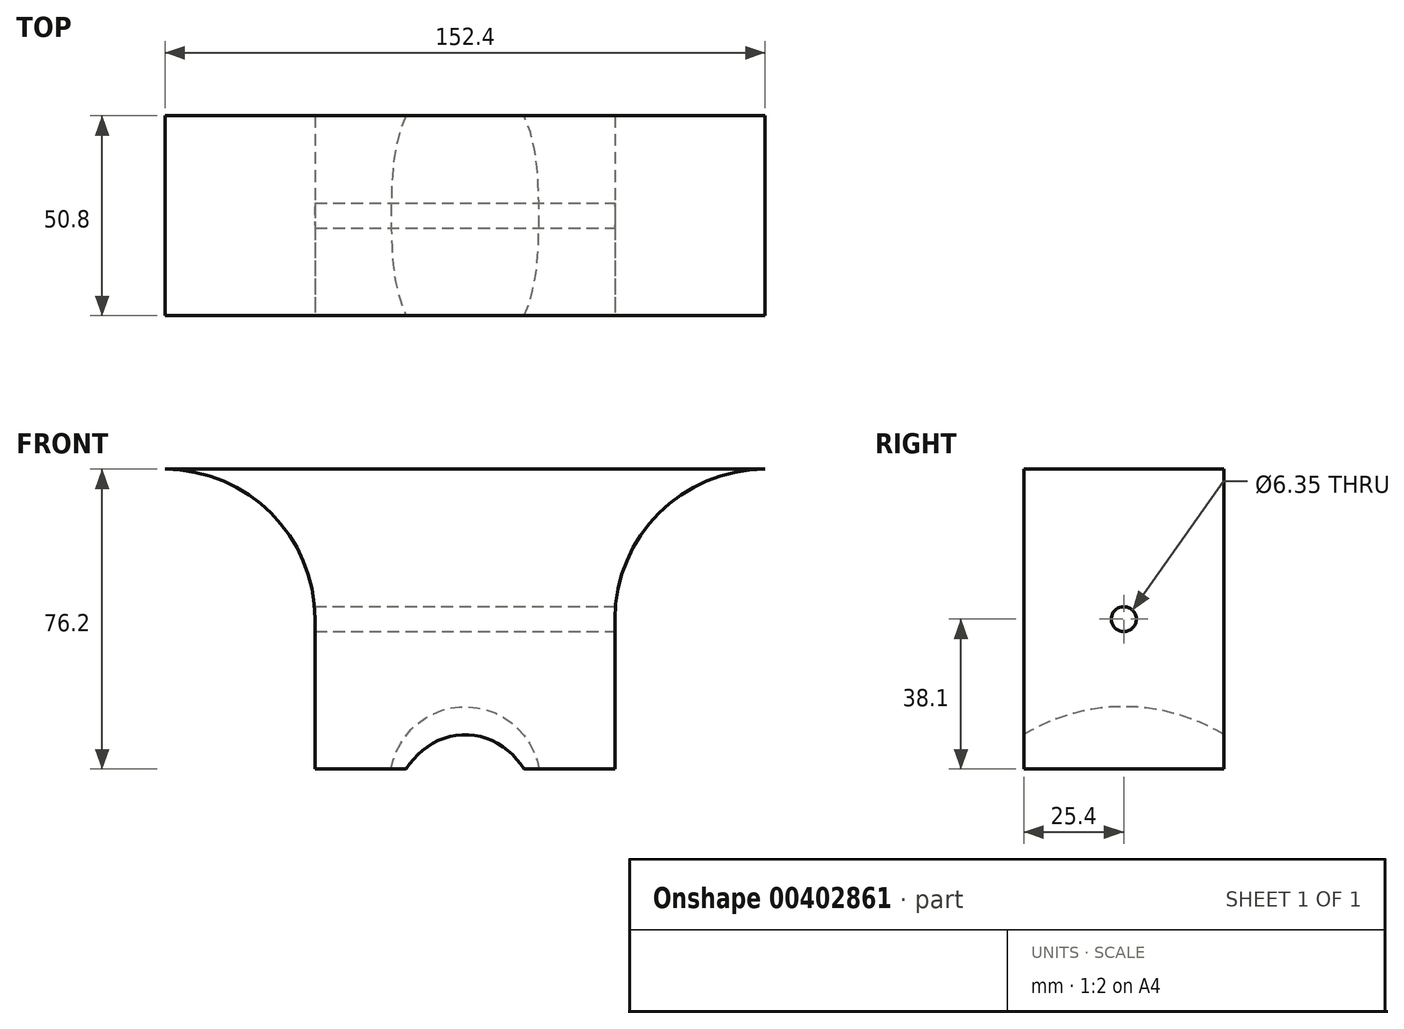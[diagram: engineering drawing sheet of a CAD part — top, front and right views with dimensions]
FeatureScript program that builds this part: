
annotation { "Feature Type Name" : "Feature", "Feature Type Description" : "" }
export const myFeature = defineFeature(function(context is Context, id is Id, definition is map)
    precondition{}
    {
        {
            var Q0;
            Q0=qCreatedBy(makeId("Front.planeOp"),FACE);
            var sketch = newSketch(context, id + "F0", { "sketchPlane" : qUnion([Q0])});
            skLineSegment(sketch, "E0.bottom", {"start": v(76.2, 38.1) * mm, "end": v(-76.2, 38.1) * mm});
            skLineSegment(sketch, "E0.top", {"start": v(76.2, -38.1) * mm, "end": v(-76.2, -38.1) * mm});
            skLineSegment(sketch, "E0.left", {"start": v(76.2, 38.1) * mm, "end": v(76.2, -38.1) * mm});
            skLineSegment(sketch, "E0.right", {"start": v(-76.2, 38.1) * mm, "end": v(-76.2, -38.1) * mm});
            skPoint(sketch, "E0.middle", {"position": v(0, 0) * mm});
            skSolve(sketch);
        }
        {
            var Q0;
            Q0 = qSketchRegion(id + "F0", true);
            extrude(context, id + "F1", {"entities" : qUnion([Q0]), "endBound" : BoundingType.SYMMETRIC, "oppositeDirection" : true, "depth" : 50.8 * mm});
        }
        {
            var Q0;
            Q0=makeQuery(id+"F1.opExtrude","CAP_FACE",FACE,{"disambiguationData":[OSD([sQuery(id+"F0.wireOp",EDGE,"E0.bottom"),sQuery(id+"F0.wireOp",EDGE,"E0.top"),sQuery(id+"F0.wireOp",EDGE,"E0.left"),sQuery(id+"F0.wireOp",EDGE,"E0.right")])],"isStart":true});
            var sketch = newSketch(context, id + "F2", { "sketchPlane" : qUnion([Q0])});
            skPoint(sketch, "E1", {"position": v(76.2, 0) * mm});
            skArc(sketch, "E2", {"start": v(76.2, 38.1) * mm, "mid": v(49.26, 26.94) * mm, "end": v(38.1, 0) * mm});
            skLineSegment(sketch, "E3", {"start": v(38.1, 0) * mm, "end": v(38.1, -38.1) * mm});
            skLineSegment(sketch, "E4", {"start": v(76.2, 38.1) * mm, "end": v(76.2, 0) * mm});
            skPoint(sketch, "E4.startSnap0", {"position": v(76.2, 38.1) * mm});
            skPoint(sketch, "E5.orphan", {"position": v(114.3, 0) * mm});
            skLineSegment(sketch, "E6", {"start": v(0, 0) * mm, "end": v(0, 46.22) * mm, "construction": true});
            skLineSegment(sketch, "E7", {"start": v(76.2, 38.1) * mm, "end": v(76.2, -38.1) * mm});
            skPoint(sketch, "E7.endSnap0", {"position": v(76.2, 19.05) * mm});
            skLineSegment(sketch, "E8", {"start": v(76.2, -38.1) * mm, "end": v(38.1, -38.1) * mm});
            skLineSegment(sketch, "E9.MirrorCS", {"start": v(-76.2, 38.1) * mm, "end": v(-76.2, 0) * mm});
            skPoint(sketch, "E10.MirrorP", {"position": v(-76.2, 0) * mm});
            skLineSegment(sketch, "E11.MirrorCS", {"start": v(-76.2, 38.1) * mm, "end": v(-76.2, -38.1) * mm});
            skPoint(sketch, "E12.MirrorP", {"position": v(-76.2, 19.05) * mm});
            skLineSegment(sketch, "E13.MirrorCS", {"start": v(-76.2, -38.1) * mm, "end": v(-38.1, -38.1) * mm});
            skLineSegment(sketch, "E14.MirrorCS", {"start": v(-38.1, 0) * mm, "end": v(-38.1, -38.1) * mm});
            skPoint(sketch, "E15.MirrorP", {"position": v(-76.2, 38.1) * mm});
            skArc(sketch, "E16.MirrorCS", {"start": v(-76.2, 38.1) * mm, "mid": v(-49.26, 26.94) * mm, "end": v(-38.1, 0) * mm});
            skSolve(sketch);
        }
        {
            var Q0;
            Q0 = qSketchRegion(id + "F2", true);
            extrude(context, id + "F3", {"entities" : qUnion([Q0]), "operationType" : NewBodyOperationType.REMOVE, "endBound" : BoundingType.THROUGH_ALL, "oppositeDirection" : true, "depth" : 25.4 * mm});
        }
        {
            var Q0;
            Q0=qCreatedBy(makeId("Right.planeOp"),FACE);
            var sketch = newSketch(context, id + "F4", { "sketchPlane" : qUnion([Q0])});
            skCircle(sketch, "E17", {"center": v(0, 0) * mm, "radius": 3.18 * mm});
            skSolve(sketch);
        }
        {
            var Q0;
            Q0 = qSketchRegion(id + "F4", true);
            extrude(context, id + "F5", {"entities" : qUnion([Q0]), "operationType" : NewBodyOperationType.REMOVE, "endBound" : BoundingType.SYMMETRIC, "oppositeDirection" : true, "depth" : 152.4 * mm});
        }
        {
            var Q0;
            Q0=qCreatedBy(makeId("Front.planeOp"),FACE);
            var sketch = newSketch(context, id + "F6", { "sketchPlane" : qUnion([Q0])});
            skPoint(sketch, "E18", {"position": v(0, -38.1) * mm});
            skLineSegment(sketch, "E19.0", {"start": v(38.1, -38.1) * mm, "end": v(-38.1, -38.1) * mm, "construction": true});
            skCircle(sketch, "E20", {"center": v(0, -41.27) * mm, "radius": 19.05 * mm});
            skLineSegment(sketch, "E21", {"start": v(-17.72, -71.12) * mm, "end": v(15.64, -71.12) * mm, "construction": true});
            skSolve(sketch);
        }
        {
            var Q0;
            Q0 = qSketchRegion(id + "F6", true);
            var Q1;
            Q1=sQuery(id+"F6.wireOp",EDGE,"E21");
            revolve(context, id + "F7", {"operationType" : NewBodyOperationType.REMOVE, "entities" : qUnion([Q0]), "axis" : qUnion([Q1]), "revolveType" : RevolveType.FULL, "oppositeDirection" : true});
        }
    });
